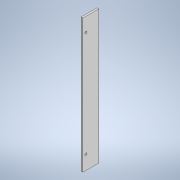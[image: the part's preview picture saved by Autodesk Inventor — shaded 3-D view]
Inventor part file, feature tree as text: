
AUTODESK INVENTOR PART (.ipt)
format: ipt  version: 2021 (Build 250183000, 183)  size: 103,424 bytes
history: native  units: mm
features: extrude x1, sketch x1
ambient origin geometry x8: Origin, YZ Plane, XZ Plane, XY Plane, X Axis, Y Axis, Z Axis, Center Point
bodies: Solid1 (feature_tree)
feature tree (2):
  extrude  "Extrusion1"  Depth=2.6mm TaperAngle=0.0deg
  sketch  "Sketch1"  dims[d0=150.0mm d1=180.0deg d2=3.2mm d3=3.2mm d4=20.0mm d5=22.7mm d6=90.0deg d7=190.0mm d8=90.0deg d9=22.7mm d10=90.0deg d11=2.6mm d12=0.0mm]
